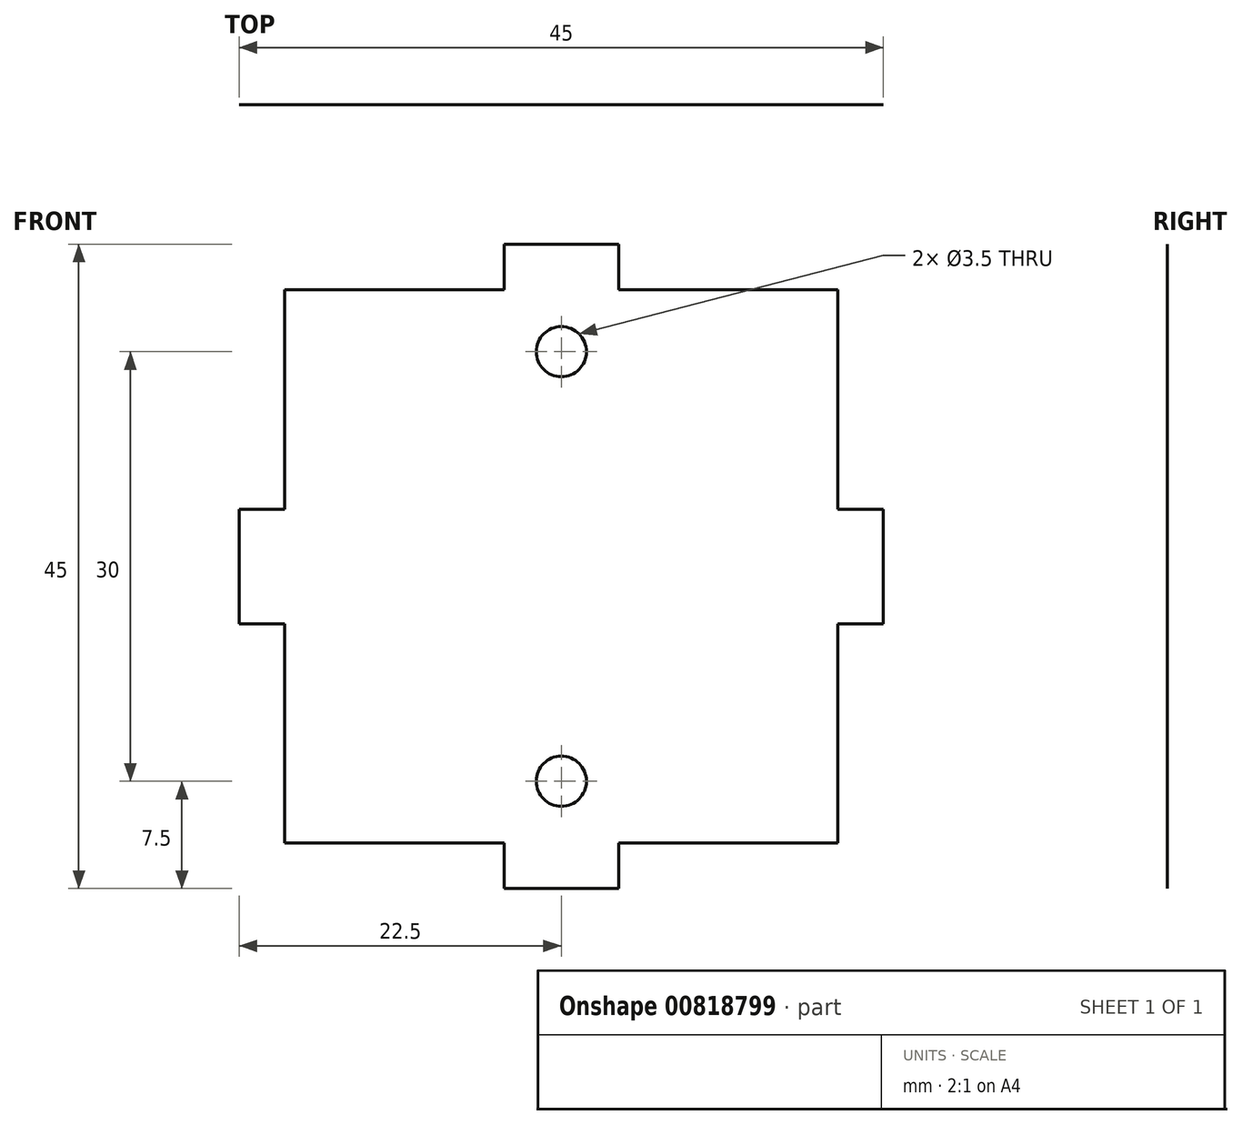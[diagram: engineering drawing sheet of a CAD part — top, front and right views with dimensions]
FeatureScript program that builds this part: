
annotation { "Feature Type Name" : "Feature", "Feature Type Description" : "" }
export const myFeature = defineFeature(function(context is Context, id is Id, definition is map)
    precondition{}
    {
        {
            var Q0;
            Q0=qCreatedBy(makeId("Front.planeOp"),FACE);
            var sketch = newSketch(context, id + "F0", { "sketchPlane" : qUnion([Q0])});
            skPoint(sketch, "E0.middle", {"position": v(0, 0) * mm});
            skLineSegment(sketch, "E1.bottom", {"start": v(-19.32, -4) * mm, "end": v(-22.5, -4) * mm});
            skLineSegment(sketch, "E1.top", {"start": v(-19.33, 4) * mm, "end": v(-22.5, 4) * mm});
            skLineSegment(sketch, "E1.right", {"start": v(-22.5, 4) * mm, "end": v(-22.5, -4) * mm});
            skLineSegment(sketch, "E2.top", {"start": v(-4, 22.5) * mm, "end": v(4, 22.5) * mm});
            skLineSegment(sketch, "E2.left", {"start": v(-4, 19.32) * mm, "end": v(-4, 22.5) * mm});
            skLineSegment(sketch, "E2.right", {"start": v(4, 19.32) * mm, "end": v(4, 22.5) * mm});
            skLineSegment(sketch, "E3.bottom", {"start": v(19.32, 4) * mm, "end": v(22.5, 4) * mm});
            skLineSegment(sketch, "E3.top", {"start": v(19.33, -4) * mm, "end": v(22.5, -4) * mm});
            skLineSegment(sketch, "E3.right", {"start": v(22.5, 4) * mm, "end": v(22.5, -4) * mm});
            skLineSegment(sketch, "E4.top", {"start": v(-4, -22.5) * mm, "end": v(4, -22.5) * mm});
            skLineSegment(sketch, "E4.left", {"start": v(-4, -19.33) * mm, "end": v(-4, -22.5) * mm});
            skLineSegment(sketch, "E4.right", {"start": v(4, -19.33) * mm, "end": v(4, -22.5) * mm});
            skPoint(sketch, "E5", {"position": v(-22.5, 0) * mm});
            skPoint(sketch, "E6", {"position": v(22.5, 0) * mm});
            skLineSegment(sketch, "E7", {"start": v(-22.5, 0) * mm, "end": v(22.5, 0) * mm});
            skPoint(sketch, "E8", {"position": v(0, 22.5) * mm});
            skPoint(sketch, "E9", {"position": v(0, -22.5) * mm});
            skLineSegment(sketch, "E10", {"start": v(0, 22.5) * mm, "end": v(0, -22.5) * mm});
            skLineSegment(sketch, "E11.bottom", {"start": v(18, -18) * mm, "end": v(-18, -18) * mm});
            skLineSegment(sketch, "E11.top", {"start": v(18, 18) * mm, "end": v(-18, 18) * mm});
            skLineSegment(sketch, "E11.left", {"start": v(18, -18) * mm, "end": v(18, 18) * mm});
            skLineSegment(sketch, "E11.right", {"start": v(-18, -18) * mm, "end": v(-18, 18) * mm});
            skCircle(sketch, "E12", {"center": v(0, 15) * mm, "radius": 1.75 * mm});
            skCircle(sketch, "E13", {"center": v(0, -15) * mm, "radius": 1.75 * mm});
            skLineSegment(sketch, "E14", {"start": v(0, 15) * mm, "end": v(0, -15) * mm});
            skLineSegment(sketch, "E15", {"start": v(-19.33, 19.32) * mm, "end": v(-19.33, 4) * mm});
            skLineSegment(sketch, "E16", {"start": v(-19.33, -4) * mm, "end": v(-19.32, -19.33) * mm});
            skLineSegment(sketch, "E17", {"start": v(19.33, -4) * mm, "end": v(19.33, -19.33) * mm});
            skLineSegment(sketch, "E18", {"start": v(19.32, 4) * mm, "end": v(19.32, 19.33) * mm});
            skLineSegment(sketch, "E19", {"start": v(-19.33, 19.32) * mm, "end": v(-4, 19.32) * mm});
            skLineSegment(sketch, "E20", {"start": v(4, 19.32) * mm, "end": v(19.32, 19.33) * mm});
            skLineSegment(sketch, "E21", {"start": v(-19.32, -19.33) * mm, "end": v(-4, -19.33) * mm});
            skLineSegment(sketch, "E22", {"start": v(4, -19.33) * mm, "end": v(19.33, -19.33) * mm});
            skSolve(sketch);
        }
        {
            var Q0;
            Q0 = qSketchRegion(id + "F0", true);
            var Q1;
            {var subQ0=sQuery(id+"F0.wireOp",EDGE,"E11.right");var subQ3=sQuery(id+"F0.wireOp",EDGE,"E7");var subQ4=makeQuery(id+"F0.imprint","INTERSECT",VERTEX,{"derivedFrom":[subQ3,subQ0]});Q1=makeQuery(id+"F0.imprint","IMPRINT",FACE,{"disambiguationData":[TD([[makeQuery(id+"F0.imprint","IMPRINT",EDGE,{"disambiguationData":[TD([[subQ4,-1.0]])],"derivedFrom":subQ3}),1.0]])]});}
            var Q2;
            {var subQ3=sQuery(id+"F0.wireOp",EDGE,"E7");var subQ9=sQuery(id+"F0.wireOp",EDGE,"E14");var subQ10=makeQuery(id+"F0.imprint","INTERSECT",VERTEX,{"derivedFrom":[subQ3,subQ9]});Q2=makeQuery(id+"F0.imprint","IMPRINT",FACE,{"disambiguationData":[TD([[makeQuery(id+"F0.imprint","IMPRINT",EDGE,{"disambiguationData":[TD([[subQ10,-1.0]])],"derivedFrom":subQ3}),1.0]])]});}
            var Q3;
            {var subQ5=sQuery(id+"F0.wireOp",EDGE,"E14");var subQ6=sQuery(id+"F0.wireOp",EDGE,"E7");var subQ7=makeQuery(id+"F0.imprint","INTERSECT",VERTEX,{"derivedFrom":[subQ6,subQ5]});Q3=makeQuery(id+"F0.imprint","IMPRINT",FACE,{"disambiguationData":[TD([[makeQuery(id+"F0.imprint","IMPRINT",EDGE,{"disambiguationData":[TD([[subQ7,-1.0]])],"derivedFrom":subQ6}),-1.0]])]});}
            var Q4;
            {var subQ0=sQuery(id+"F0.wireOp",EDGE,"E11.right");var subQ3=sQuery(id+"F0.wireOp",EDGE,"E7");var subQ4=makeQuery(id+"F0.imprint","INTERSECT",VERTEX,{"derivedFrom":[subQ3,subQ0]});Q4=makeQuery(id+"F0.imprint","IMPRINT",FACE,{"disambiguationData":[TD([[makeQuery(id+"F0.imprint","IMPRINT",EDGE,{"disambiguationData":[TD([[subQ4,-1.0]])],"derivedFrom":subQ3}),-1.0]])]});}
            extrude(context, id + "F1", {"entities" : qUnion([Q0, Q1, Q2, Q3, Q4]), "depth" : 1 / 203.2 * mm, "offsetDistance" : 25 * mm});
        }
    });
